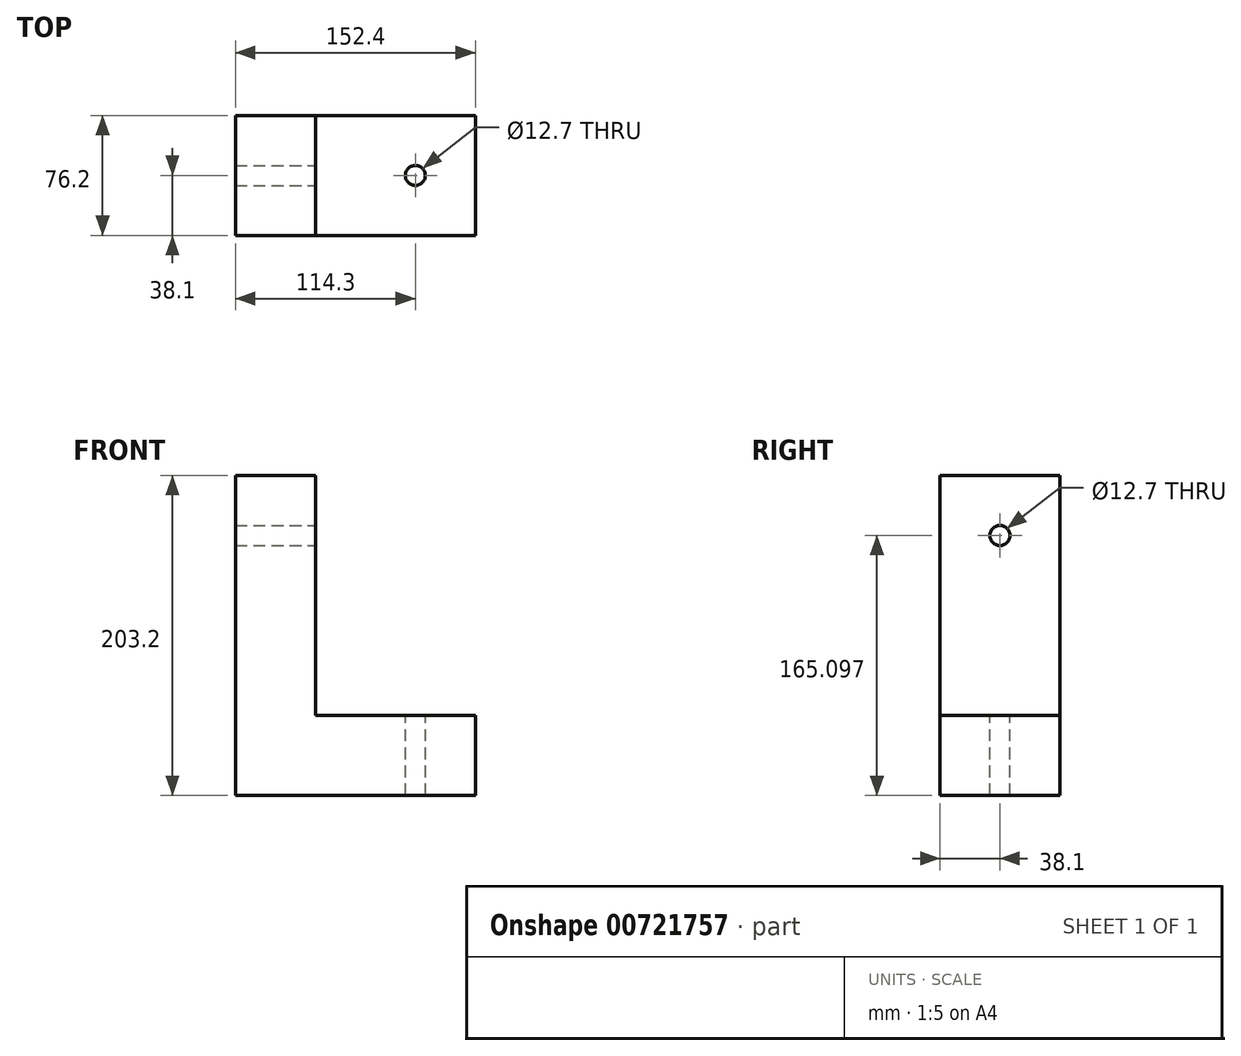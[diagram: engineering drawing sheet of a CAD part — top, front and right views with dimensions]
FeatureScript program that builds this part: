
annotation { "Feature Type Name" : "Feature", "Feature Type Description" : "" }
export const myFeature = defineFeature(function(context is Context, id is Id, definition is map)
    precondition{}
    {
        {
            var Q0;
            Q0=qCreatedBy(makeId("Front.planeOp"),FACE);
            var sketch = newSketch(context, id + "F0", { "sketchPlane" : qUnion([Q0])});
            skLineSegment(sketch, "E0", {"start": v(-50.8, 103.47) * mm, "end": v(-50.8, -99.73) * mm});
            skLineSegment(sketch, "E1", {"start": v(0, 103.47) * mm, "end": v(-50.8, 103.47) * mm});
            skLineSegment(sketch, "E2", {"start": v(-50.8, -99.73) * mm, "end": v(101.6, -99.73) * mm});
            skLineSegment(sketch, "E3", {"start": v(101.6, -99.73) * mm, "end": v(101.6, -48.93) * mm});
            skLineSegment(sketch, "E4", {"start": v(0, -48.93) * mm, "end": v(101.6, -48.93) * mm});
            skLineSegment(sketch, "E5", {"start": v(0, 103.47) * mm, "end": v(0, -48.93) * mm});
            skSolve(sketch);
        }
        {
            var Q0;
            Q0=makeQuery(id+"F0.imprint","IMPRINT",FACE,{"disambiguationData":[TD([[makeQuery(id+"F0.imprint","IMPRINT",EDGE,{"derivedFrom":sQuery(id+"F0.wireOp",EDGE,"E0")}),1.0]])]});
            extrude(context, id + "F1", {"entities" : qUnion([Q0]), "depth" : 76.2 * mm, "offsetDistance" : 25.4 * mm});
        }
        {
            var Q0;
            Q0=makeQuery(id+"F1.opExtrude","SWEPT_FACE",FACE,{"disambiguationData":[OSD([sQuery(id+"F0.wireOp",EDGE,"E5")])]});
            var sketch = newSketch(context, id + "F2", { "sketchPlane" : qUnion([Q0])});
            skSolve(sketch);
        }
        {
            var Q0;
            {var subQ0=sQuery(id+"F0.wireOp",EDGE,"E5");Q0=makeQuery(id+"F2.imprint","IMPRINT",FACE,{"disambiguationData":[TD([[makeQuery(id+"F2.imprint","IMPRINT",EDGE,{"derivedFrom":makeQuery(id+"F1.opExtrude","CAP_EDGE",EDGE,{"disambiguationData":[OSD([subQ0])],"isStart":true})}),-1.0]])]});}
            var sketch = newSketch(context, id + "F3", { "sketchPlane" : qUnion([Q0])});
            skCircle(sketch, "E6", {"center": v(-38.1, 65.37) * mm, "radius": 6.35 * mm});
            skSolve(sketch);
        }
        {
            var Q0;
            Q0=sQuery(id+"F3.wireOp",VERTEX,"E6.center");
            var Q1;
            Q1=makeQuery(id+"F1.opExtrude","SWEPT_BODY",BODY,{"disambiguationData":[OSD([sQuery(id+"F0.wireOp",EDGE,"E0"),sQuery(id+"F0.wireOp",EDGE,"E1"),sQuery(id+"F0.wireOp",EDGE,"E2"),sQuery(id+"F0.wireOp",EDGE,"E3"),sQuery(id+"F0.wireOp",EDGE,"E4"),sQuery(id+"F0.wireOp",EDGE,"E5")])]});
            hole(context, id + "F4", {"style" : HoleStyle.SIMPLE, "endStyle" : HoleEndStyle.THROUGH, "holeDiameter" : 12.7 * mm, "majorDiameter" : 6.35 * mm, "isTappedThrough" : true, "tappedDepth" : 12.7 * mm, "tapClearance" : 3, "locations" : qUnion([Q0]), "scope" : qUnion([Q1])});
        }
        {
            var Q0;
            Q0=makeQuery(id+"F1.opExtrude","SWEPT_FACE",FACE,{"disambiguationData":[OSD([sQuery(id+"F0.wireOp",EDGE,"E4")])]});
            var sketch = newSketch(context, id + "F5", { "sketchPlane" : qUnion([Q0])});
            skCircle(sketch, "E7", {"center": v(63.5, -38.1) * mm, "radius": 6.35 * mm});
            skSolve(sketch);
        }
        {
            var Q0;
            Q0=sQuery(id+"F5.wireOp",VERTEX,"E7.center");
            var Q1;
            Q1=makeQuery(id+"F1.opExtrude","SWEPT_BODY",BODY,{"disambiguationData":[OSD([sQuery(id+"F0.wireOp",EDGE,"E0"),sQuery(id+"F0.wireOp",EDGE,"E1"),sQuery(id+"F0.wireOp",EDGE,"E2"),sQuery(id+"F0.wireOp",EDGE,"E3"),sQuery(id+"F0.wireOp",EDGE,"E4"),sQuery(id+"F0.wireOp",EDGE,"E5")])]});
            hole(context, id + "F6", {"style" : HoleStyle.SIMPLE, "endStyle" : HoleEndStyle.THROUGH, "holeDiameter" : 12.7 * mm, "majorDiameter" : 6.35 * mm, "isTappedThrough" : true, "tappedDepth" : 12.7 * mm, "tapClearance" : 3, "locations" : qUnion([Q0]), "scope" : qUnion([Q1])});
        }
    });
